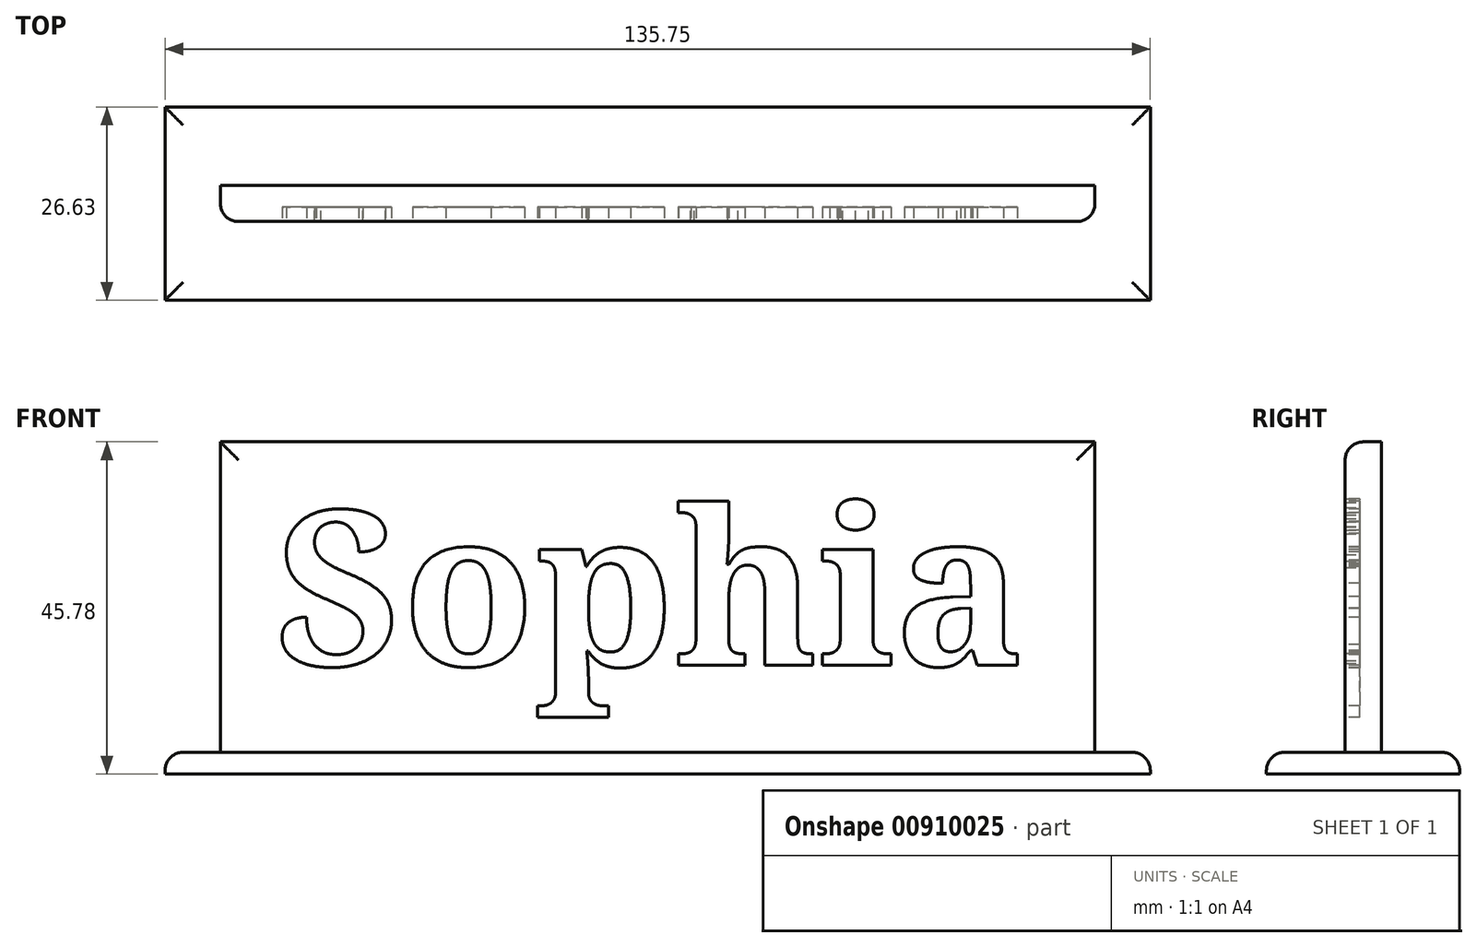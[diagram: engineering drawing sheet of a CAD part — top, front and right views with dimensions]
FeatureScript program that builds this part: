
annotation { "Feature Type Name" : "Feature", "Feature Type Description" : "" }
export const myFeature = defineFeature(function(context is Context, id is Id, definition is map)
    precondition{}
    {
        {
            var Q0;
            Q0=qCreatedBy(makeId("Front.planeOp"),FACE);
            var sketch = newSketch(context, id + "F0", { "sketchPlane" : qUnion([Q0])});
            skLineSegment(sketch, "E0.bottom", {"start": v(-54.51, 50.5) * mm, "end": v(65.98, 50.5) * mm});
            skLineSegment(sketch, "E0.top", {"start": v(-54.51, 7.72) * mm, "end": v(65.98, 7.72) * mm});
            skLineSegment(sketch, "E0.left", {"start": v(-54.51, 50.5) * mm, "end": v(-54.51, 7.72) * mm});
            skLineSegment(sketch, "E0.right", {"start": v(65.98, 50.5) * mm, "end": v(65.98, 7.72) * mm});
            skSolve(sketch);
        }
        {
            var Q0;
            Q0=makeQuery(id+"F0.imprint","IMPRINT",FACE,{"disambiguationData":[TD([[makeQuery(id+"F0.imprint","IMPRINT",EDGE,{"derivedFrom":sQuery(id+"F0.wireOp",EDGE,"E0.bottom")}),-1.0]])]});
            extrude(context, id + "F1", {"entities" : qUnion([Q0]), "oppositeDirection" : true, "depth" : 5 * mm, "offsetDistance" : 25 * mm});
        }
        {
            var Q0;
            Q0=qCreatedBy(makeId("Front.planeOp"),FACE);
            var sketch = newSketch(context, id + "F2", { "sketchPlane" : qUnion([Q0])});
            skText(sketch, "E1", { "text": "Sophia", "fontName": "NotoSerif-Bold.ttf"});
            const initialGuessF2  = {"E1": [-0.0469, 0.01969, 1, 0, 0.02145]};
            skSetInitialGuess(sketch, initialGuessF2);
            skSolve(sketch);
        }
        {
            var Q0;
            Q0 = qSketchRegion(id + "F2", true);
            extrude(context, id + "F3", {"entities" : qUnion([Q0]), "operationType" : NewBodyOperationType.REMOVE, "oppositeDirection" : true, "depth" : 2 * mm, "offsetDistance" : 25 * mm});
        }
        {
            var Q0;
            Q0=makeQuery(id+"F1.opExtrude","SWEPT_FACE",FACE,{"disambiguationData":[OSD([sQuery(id+"F0.wireOp",EDGE,"E0.top")])]});
            var sketch = newSketch(context, id + "F4", { "sketchPlane" : qUnion([Q0])});
            skLineSegment(sketch, "E2.bottom", {"start": v(-62.14, 10.84) * mm, "end": v(73.61, 10.84) * mm});
            skLineSegment(sketch, "E2.top", {"start": v(-62.14, -15.79) * mm, "end": v(73.61, -15.79) * mm});
            skLineSegment(sketch, "E2.left", {"start": v(-62.14, 10.84) * mm, "end": v(-62.14, -15.79) * mm});
            skLineSegment(sketch, "E2.right", {"start": v(73.61, 10.84) * mm, "end": v(73.61, -15.79) * mm});
            skPoint(sketch, "E2.middle", {"position": v(5.73, -2.47) * mm});
            skPoint(sketch, "E2.middle.positionSnap0", {"position": v(5.73, 0) * mm});
            skPoint(sketch, "E2.centerSnap0", {"position": v(5.73, 0) * mm});
            skSolve(sketch);
        }
        {
            var Q0;
            Q0=makeQuery(id+"F4.imprint","IMPRINT",FACE,{"disambiguationData":[TD([[makeQuery(id+"F4.imprint","IMPRINT",EDGE,{"derivedFrom":sQuery(id+"F4.wireOp",EDGE,"E2.bottom")}),-1.0]])]});
            var Q1;
            {var subQ0=sQuery(id+"F0.wireOp",EDGE,"E0.top");Q1=makeQuery(id+"F4.imprint","IMPRINT",FACE,{"disambiguationData":[TD([[makeQuery(id+"F4.imprint","IMPRINT",EDGE,{"derivedFrom":makeQuery(id+"F1.opExtrude","CAP_EDGE",EDGE,{"disambiguationData":[OSD([subQ0])],"isStart":true})}),-1.0]])]});}
            extrude(context, id + "F5", {"entities" : qUnion([Q0, Q1]), "depth" : 3 * mm, "offsetDistance" : 25 * mm});
        }
        {
            var Q0;
            Q0=makeQuery(id+"F1.opExtrude","CAP_EDGE",EDGE,{"disambiguationData":[OSD([sQuery(id+"F0.wireOp",EDGE,"E0.bottom")])],"isStart":true});
            var Q1;
            Q1=makeQuery(id+"F1.opExtrude","CAP_EDGE",EDGE,{"disambiguationData":[OSD([sQuery(id+"F0.wireOp",EDGE,"E0.left")])],"isStart":true});
            var Q2;
            Q2=makeQuery(id+"F1.opExtrude","CAP_EDGE",EDGE,{"disambiguationData":[OSD([sQuery(id+"F0.wireOp",EDGE,"E0.right")])],"isStart":true});
            var Q3;
            Q3=makeQuery(id+"F5.opExtrude","CAP_FACE",FACE,{"disambiguationData":[OSD([sQuery(id+"F0.wireOp",EDGE,"E0.top"),sQuery(id+"F0.wireOp",EDGE,"E0.left"),sQuery(id+"F0.wireOp",EDGE,"E0.right"),sQuery(id+"F4.wireOp",EDGE,"E2.bottom"),sQuery(id+"F4.wireOp",EDGE,"E2.top"),sQuery(id+"F4.wireOp",EDGE,"E2.left"),sQuery(id+"F4.wireOp",EDGE,"E2.right")])],"isStart":true});
            fillet(context, id + "F6", {"entities" : qUnion([Q0, Q1, Q2, Q3]), "radius" : 2.5 * mm, "tangentPropagation" : true, "allowEdgeOverflow" : false});
        }
    });
